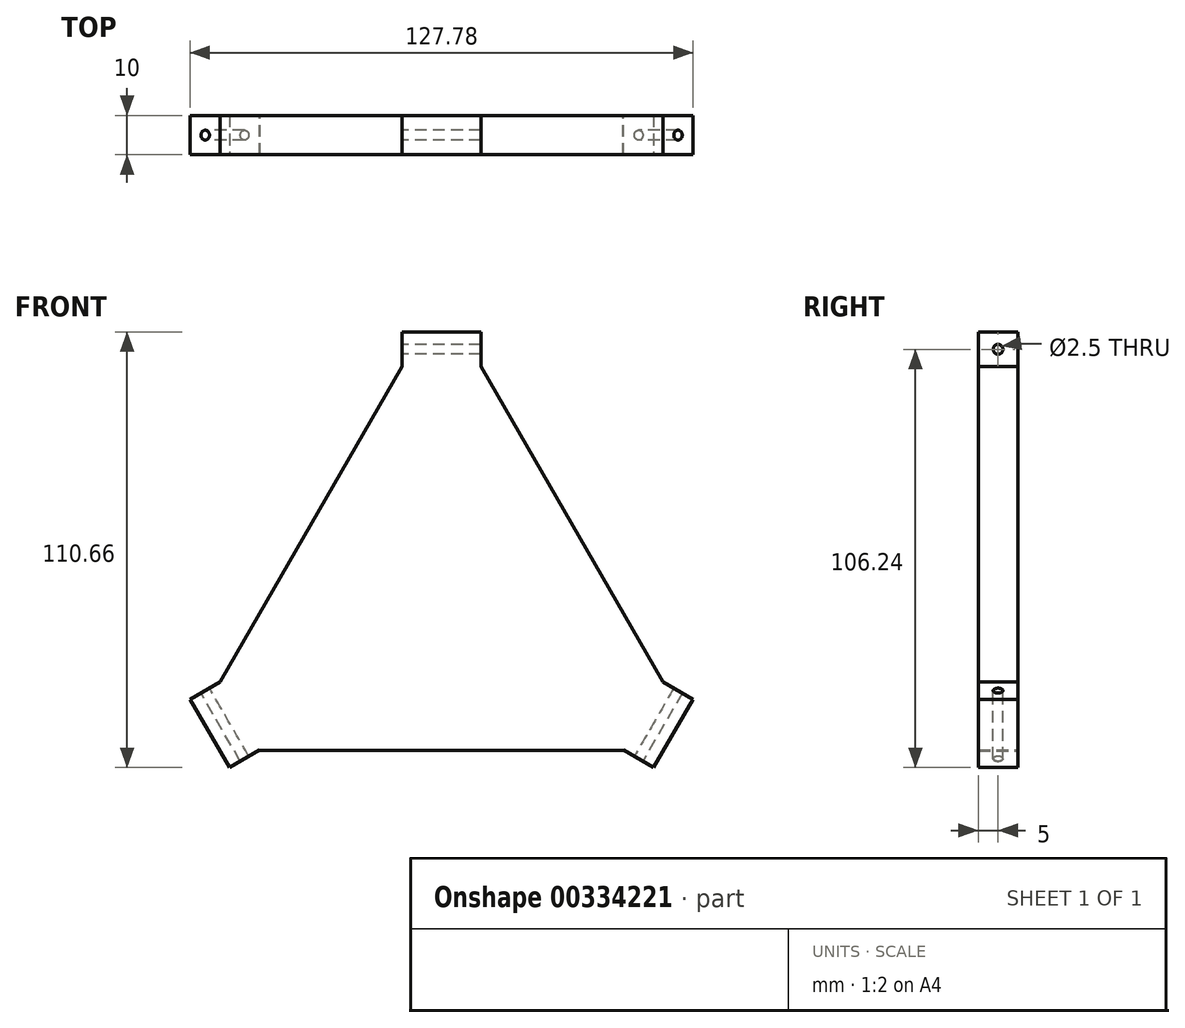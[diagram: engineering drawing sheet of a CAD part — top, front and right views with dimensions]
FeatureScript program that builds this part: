
annotation { "Feature Type Name" : "Feature", "Feature Type Description" : "" }
export const myFeature = defineFeature(function(context is Context, id is Id, definition is map)
    precondition{}
    {
        {
            var Q0;
            Q0=qCreatedBy(makeId("Front.planeOp"),FACE);
            var sketch = newSketch(context, id + "F0", { "sketchPlane" : qUnion([Q0])});
            skLineSegment(sketch, "E0", {"start": v(78.9, 0) * mm, "end": v(-99.14, 0) * mm, "construction": true});
            skLineSegment(sketch, "E1", {"start": v(0, 0) * mm, "end": v(-68.33, -39.45) * mm, "construction": true});
            skLineSegment(sketch, "E2", {"start": v(0, 0) * mm, "end": v(228.8, -132.1) * mm, "construction": true});
            skLineSegment(sketch, "E3", {"start": v(0, 58.9) * mm, "end": v(0, -87.18) * mm, "construction": true});
            skCircle(sketch, "E4", {"center": v(0, 0) * mm, "radius": 60 * mm});
            skSolve(sketch);
        }
        {
            var Q0;
            Q0 = qSketchRegion(id + "F0", true);
            extrude(context, id + "F1", {"entities" : qUnion([Q0]), "depth" : 10 * mm});
        }
        {
            var Q0;
            Q0=makeQuery(id+"F1.opExtrude","CAP_FACE",FACE,{"disambiguationData":[OSD([sQuery(id+"F0.wireOp",EDGE,"E4")])],"isStart":false});
            var sketch = newSketch(context, id + "F2", { "sketchPlane" : qUnion([Q0])});
            skLineSegment(sketch, "E5", {"start": v(0, 60) * mm, "end": v(0, -57.07) * mm, "construction": true});
            skLineSegment(sketch, "E6.bottom", {"start": v(-10, 68) * mm, "end": v(10, 68) * mm});
            skLineSegment(sketch, "E6.top", {"start": v(-10, 58) * mm, "end": v(10, 58) * mm});
            skLineSegment(sketch, "E6.left", {"start": v(-10, 68) * mm, "end": v(-10, 58) * mm});
            skLineSegment(sketch, "E6.right", {"start": v(10, 68) * mm, "end": v(10, 58) * mm});
            skLineSegment(sketch, "E7", {"start": v(-60, 0) * mm, "end": v(60, 0) * mm, "construction": true});
            skLineSegment(sketch, "E8.1.0", {"start": v(-45.23, -37.66) * mm, "end": v(-55.23, -20.34) * mm});
            skLineSegment(sketch, "E8.1.1", {"start": v(-53.89, -42.66) * mm, "end": v(-63.89, -25.34) * mm});
            skLineSegment(sketch, "E8.1.2", {"start": v(-53.89, -42.66) * mm, "end": v(-45.23, -37.66) * mm});
            skLineSegment(sketch, "E8.1.3", {"start": v(-63.89, -25.34) * mm, "end": v(-55.23, -20.34) * mm});
            skLineSegment(sketch, "E8.2.0", {"start": v(55.23, -20.34) * mm, "end": v(45.23, -37.66) * mm});
            skLineSegment(sketch, "E8.2.1", {"start": v(63.89, -25.34) * mm, "end": v(53.89, -42.66) * mm});
            skLineSegment(sketch, "E8.2.2", {"start": v(63.89, -25.34) * mm, "end": v(55.23, -20.34) * mm});
            skLineSegment(sketch, "E8.2.3", {"start": v(53.89, -42.66) * mm, "end": v(45.23, -37.66) * mm});
            skPoint(sketch, "E8.center", {"position": v(0, 0) * mm});
            skSolve(sketch);
        }
        {
            var Q0;
            Q0 = qSketchRegion(id + "F2", true);
            extrude(context, id + "F3", {"entities" : qUnion([Q0]), "operationType" : NewBodyOperationType.ADD, "oppositeDirection" : true, "depth" : 10 * mm});
        }
        {
            var Q0;
            Q0=makeQuery(id+"F3.opExtrude","SWEPT_FACE",FACE,{"disambiguationData":[OSD([sQuery(id+"F2.wireOp",EDGE,"E6.left")])]});
            var sketch = newSketch(context, id + "F4", { "sketchPlane" : qUnion([Q0])});
            skLineSegment(sketch, "E9", {"start": v(5, 68) * mm, "end": v(5, 53.3) * mm, "construction": true});
            skPoint(sketch, "E9.endSnap0", {"position": v(5, 68) * mm});
            skLineSegment(sketch, "E10", {"start": v(5, 53.3) * mm, "end": v(10, 63.58) * mm, "construction": true});
            skLineSegment(sketch, "E11", {"start": v(10, 63.58) * mm, "end": v(-2.25, 63.58) * mm, "construction": true});
            skPoint(sketch, "E12", {"position": v(5, 63.58) * mm});
            skSolve(sketch);
        }
        {
            var Q0;
            Q0=sQuery(id+"F4.wireOp",VERTEX,"E12");
            var Q1;
            Q1=makeQuery(id+"F1.opExtrude","SWEPT_BODY",BODY,{"disambiguationData":[OSD([sQuery(id+"F0.wireOp",EDGE,"E4")])]});
            hole(context, id + "F5", {"style" : HoleStyle.SIMPLE, "endStyle" : HoleEndStyle.THROUGH, "standardTappedOrClearance" : lookupTablePath({ "standard" : "ISO", "engagement" : "75%", "pitch" : "0.5 mm", "size" : "M3", "type" : "Tapped" }), "standardBlindInLast" : lookupTablePath({ "standard" : "ISO", "engagement" : "75%", "pitch" : "0.5 mm", "size" : "M3", "type" : "Tapped" }), "holeDiameter" : 2.5 * mm, "showTappedDepth" : true, "tappedDepth" : 15 * mm, "tapClearance" : 1, "locations" : qUnion([Q0]), "scope" : qUnion([Q1]), "majorDiameter" : 3 * mm});
        }
        {
            var Q0;
            Q0=makeQuery(id+"F3.opExtrude","SWEPT_FACE",FACE,{"disambiguationData":[OSD([sQuery(id+"F2.wireOp",EDGE,"E8.1.3")])]});
            var sketch = newSketch(context, id + "F6", { "sketchPlane" : qUnion([Q0])});
            skLineSegment(sketch, "E13", {"start": v(-59.16, -5) * mm, "end": v(-75.78, -5) * mm, "construction": true});
            skLineSegment(sketch, "E14", {"start": v(-63.58, 0) * mm, "end": v(-63.58, -24.87) * mm, "construction": true});
            skPoint(sketch, "E15", {"position": v(-63.58, -5) * mm});
            skSolve(sketch);
        }
        {
            var Q0;
            Q0=sQuery(id+"F6.wireOp",VERTEX,"E15");
            var Q1;
            Q1=makeQuery(id+"F1.opExtrude","SWEPT_BODY",BODY,{"disambiguationData":[OSD([sQuery(id+"F0.wireOp",EDGE,"E4")])]});
            hole(context, id + "F7", {"style" : HoleStyle.SIMPLE, "endStyle" : HoleEndStyle.THROUGH, "standardTappedOrClearance" : lookupTablePath({ "standard" : "ISO", "engagement" : "75%", "pitch" : "0.5 mm", "size" : "M3", "type" : "Tapped" }), "standardBlindInLast" : lookupTablePath({ "standard" : "ISO", "engagement" : "75%", "pitch" : "0.5 mm", "size" : "M3", "type" : "Tapped" }), "holeDiameter" : 2.5 * mm, "showTappedDepth" : true, "tappedDepth" : 15 * mm, "tapClearance" : 1, "locations" : qUnion([Q0]), "scope" : qUnion([Q1]), "majorDiameter" : 3 * mm});
        }
        {
            var Q0;
            Q0=makeQuery(id+"F3.opExtrude","SWEPT_FACE",FACE,{"disambiguationData":[OSD([sQuery(id+"F2.wireOp",EDGE,"E8.2.3")])]});
            var sketch = newSketch(context, id + "F8", { "sketchPlane" : qUnion([Q0])});
            skLineSegment(sketch, "E16", {"start": v(68.96, 5) * mm, "end": v(54.91, 5) * mm, "construction": true});
            skPoint(sketch, "E16.startSnap0", {"position": v(68, 5) * mm});
            skLineSegment(sketch, "E17", {"start": v(54.91, 5) * mm, "end": v(63.58, 0) * mm, "construction": true});
            skLineSegment(sketch, "E18", {"start": v(63.58, 0) * mm, "end": v(63.58, 13.12) * mm, "construction": true});
            skPoint(sketch, "E19", {"position": v(63.58, 5) * mm});
            skSolve(sketch);
        }
        {
            var Q0;
            Q0=sQuery(id+"F8.wireOp",VERTEX,"E19");
            var Q1;
            Q1=makeQuery(id+"F1.opExtrude","SWEPT_BODY",BODY,{"disambiguationData":[OSD([sQuery(id+"F0.wireOp",EDGE,"E4")])]});
            hole(context, id + "F9", {"style" : HoleStyle.SIMPLE, "endStyle" : HoleEndStyle.THROUGH, "standardTappedOrClearance" : lookupTablePath({ "standard" : "ISO", "engagement" : "75%", "pitch" : "0.5 mm", "size" : "M3", "type" : "Tapped" }), "standardBlindInLast" : lookupTablePath({ "standard" : "ISO", "engagement" : "75%", "pitch" : "0.5 mm", "size" : "M3", "type" : "Tapped" }), "holeDiameter" : 2.5 * mm, "showTappedDepth" : true, "tappedDepth" : 15 * mm, "tapClearance" : 1, "locations" : qUnion([Q0]), "scope" : qUnion([Q1]), "majorDiameter" : 3 * mm});
        }
        {
            var Q0;
            Q0=makeQuery(id+"F0.imprint","IMPRINT",FACE,{"disambiguationData":[TD([[makeQuery(id+"F0.imprint","IMPRINT",EDGE,{"derivedFrom":sQuery(id+"F0.wireOp",EDGE,"E4")}),1.0]])]});
            var sketch = newSketch(context, id + "F10", { "sketchPlane" : qUnion([Q0])});
            skLineSegment(sketch, "E20", {"start": v(-46.2, -38.33) * mm, "end": v(46.06, -38.33) * mm});
            skLineSegment(sketch, "E21", {"start": v(-46.2, -38.33) * mm, "end": v(-47.86, -60.5) * mm});
            skLineSegment(sketch, "E22", {"start": v(-47.86, -60.5) * mm, "end": v(42.83, -62.1) * mm});
            skLineSegment(sketch, "E23", {"start": v(42.83, -62.1) * mm, "end": v(46.06, -38.33) * mm});
            skSolve(sketch);
        }
        {
            var Q0;
            Q0 = qSketchRegion(id + "F10", true);
            extrude(context, id + "F11", {"entities" : qUnion([Q0]), "operationType" : NewBodyOperationType.REMOVE, "endBound" : BoundingType.THROUGH_ALL, "depth" : 25 * mm});
        }
        {
            var Q0;
            Q0=makeQuery(id+"F3.boolean.opBoolean","MERGE",FACE,{"derivedFrom":[makeQuery(id+"F1.opExtrude","CAP_FACE",FACE,{"disambiguationData":[OSD([sQuery(id+"F0.wireOp",EDGE,"E4")])],"isStart":true}),makeQuery(id+"F3.opExtrude","CAP_FACE",FACE,{"disambiguationData":[OSD([sQuery(id+"F2.wireOp",EDGE,"E6.bottom"),sQuery(id+"F2.wireOp",EDGE,"E6.top"),sQuery(id+"F2.wireOp",EDGE,"E6.left"),sQuery(id+"F2.wireOp",EDGE,"E6.right")])],"isStart":false}),makeQuery(id+"F3.opExtrude","CAP_FACE",FACE,{"disambiguationData":[OSD([sQuery(id+"F2.wireOp",EDGE,"E8.1.0"),sQuery(id+"F2.wireOp",EDGE,"E8.1.1"),sQuery(id+"F2.wireOp",EDGE,"E8.1.2"),sQuery(id+"F2.wireOp",EDGE,"E8.1.3")])],"isStart":false}),makeQuery(id+"F3.opExtrude","CAP_FACE",FACE,{"disambiguationData":[OSD([sQuery(id+"F2.wireOp",EDGE,"E8.2.0"),sQuery(id+"F2.wireOp",EDGE,"E8.2.1"),sQuery(id+"F2.wireOp",EDGE,"E8.2.2"),sQuery(id+"F2.wireOp",EDGE,"E8.2.3")])],"isStart":false})]});
            var sketch = newSketch(context, id + "F12", { "sketchPlane" : qUnion([Q0])});
            skLineSegment(sketch, "E24", {"start": v(56.23, -20.92) * mm, "end": v(10, 59.16) * mm});
            skLineSegment(sketch, "E25", {"start": v(10, 59.16) * mm, "end": v(39.3, 80.5) * mm});
            skLineSegment(sketch, "E26", {"start": v(39.3, 80.5) * mm, "end": v(84.36, -9.62) * mm});
            skLineSegment(sketch, "E27", {"start": v(84.36, -9.62) * mm, "end": v(56.23, -20.92) * mm});
            skLineSegment(sketch, "E28", {"start": v(-10, 59.16) * mm, "end": v(-56.23, -20.92) * mm});
            skLineSegment(sketch, "E29", {"start": v(-56.23, -20.92) * mm, "end": v(-86.68, -3.34) * mm});
            skLineSegment(sketch, "E30", {"start": v(-86.68, -3.34) * mm, "end": v(-43.34, 71.72) * mm});
            skLineSegment(sketch, "E31", {"start": v(-43.34, 71.72) * mm, "end": v(-10, 59.16) * mm});
            skSolve(sketch);
        }
        {
            var Q0;
            Q0 = qSketchRegion(id + "F12", true);
            extrude(context, id + "F13", {"entities" : qUnion([Q0]), "operationType" : NewBodyOperationType.REMOVE, "oppositeDirection" : true, "depth" : 25 * mm});
        }
    });
